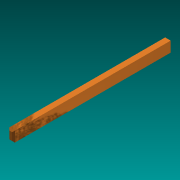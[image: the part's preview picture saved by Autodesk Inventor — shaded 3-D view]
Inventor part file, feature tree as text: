
AUTODESK INVENTOR PART (.ipt)
format: ipt  version: 2015 (Build 190159000, 159)  size: 82,944 bytes
history: native  units: mm
features: extrude x1, chamfer x1, sketch x1
ambient origin geometry x8: Origin, YZ Plane, XZ Plane, XY Plane, X Axis, Y Axis, Z Axis, Center Point
bodies: Solid1 (feature_tree)
feature tree (3):
  extrude  "Extrusion1"  Depth=0.762mm
  chamfer  "Chamfer1"  Distance=11.61mm
  sketch  "Sketch1"  dims[d0=0.4064mm d1=0.762mm d2=11.61mm d3=0.0mm d4=0.1mm d5=2.0mm d6=45.0deg]
